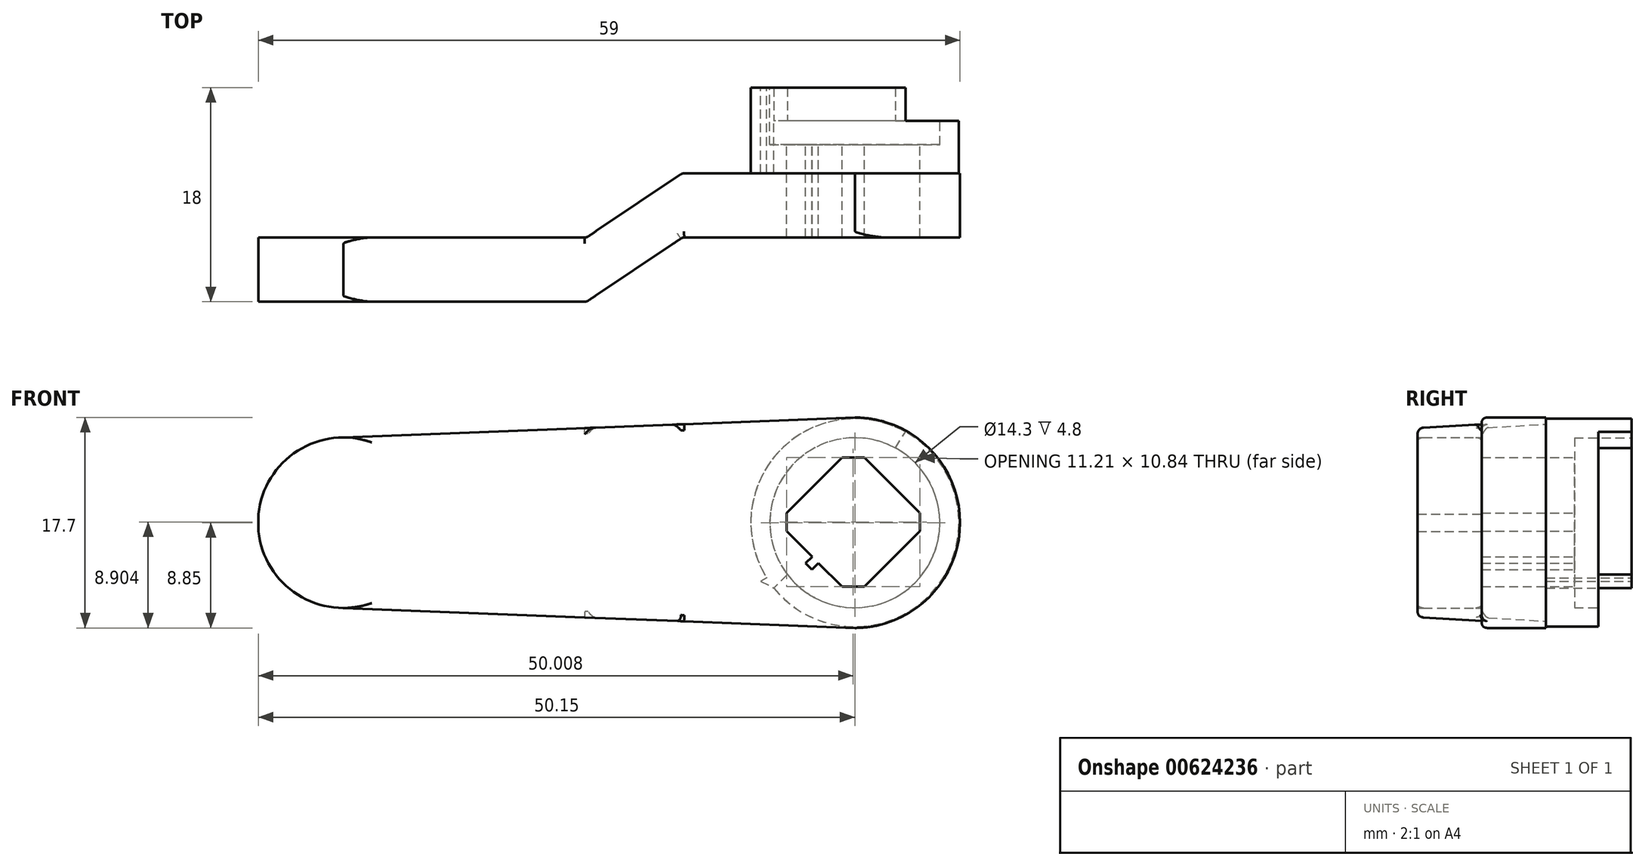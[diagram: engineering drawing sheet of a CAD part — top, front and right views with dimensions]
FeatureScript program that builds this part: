
annotation { "Feature Type Name" : "Feature", "Feature Type Description" : "" }
export const myFeature = defineFeature(function(context is Context, id is Id, definition is map)
    precondition{}
    {
        {
            var Q0;
            Q0=qCreatedBy(makeId("Top.planeOp"),FACE);
            var sketch = newSketch(context, id + "F0", { "sketchPlane" : qUnion([Q0])});
            skLineSegment(sketch, "E0", {"start": v(-29.5, 0) * mm, "end": v(29.5, 0) * mm, "construction": true});
            skLineSegment(sketch, "E1", {"start": v(0, 6.5) * mm, "end": v(0, -6.5) * mm, "construction": true});
            skLineSegment(sketch, "E2", {"start": v(-29.5, -6.5) * mm, "end": v(-29.5, -1.1) * mm});
            skLineSegment(sketch, "E3", {"start": v(-29.5, -6.5) * mm, "end": v(-1.9, -6.5) * mm});
            skLineSegment(sketch, "E4", {"start": v(-29.5, -1.1) * mm, "end": v(-1.9, -1.1) * mm});
            skLineSegment(sketch, "E5", {"start": v(-1.9, -1.1) * mm, "end": v(6.16, 4.3) * mm});
            skLineSegment(sketch, "E6", {"start": v(-1.9, -6.5) * mm, "end": v(6.16, -1.1) * mm});
            skLineSegment(sketch, "E7", {"start": v(6.16, 4.3) * mm, "end": v(29.5, 4.3) * mm});
            skLineSegment(sketch, "E8", {"start": v(29.5, 4.3) * mm, "end": v(29.5, -1.1) * mm});
            skLineSegment(sketch, "E9", {"start": v(29.5, -1.1) * mm, "end": v(6.16, -1.1) * mm});
            skSolve(sketch);
        }
        {
            var Q0;
            Q0=makeQuery(id+"F0.imprint","IMPRINT",FACE,{"disambiguationData":[TD([[makeQuery(id+"F0.imprint","IMPRINT",EDGE,{"derivedFrom":sQuery(id+"F0.wireOp",EDGE,"E2")}),-1.0]])]});
            extrude(context, id + "F1", {"entities" : qUnion([Q0]), "depth" : 17.7 * mm, "offsetDistance" : 25 * mm});
        }
        {
            var Q0;
            Q0=makeQuery(id+"F1.opExtrude","SWEPT_FACE",FACE,{"disambiguationData":[OSD([sQuery(id+"F0.wireOp",EDGE,"E7")])]});
            var sketch = newSketch(context, id + "F2", { "sketchPlane" : qUnion([Q0])});
            skLineSegment(sketch, "E10", {"start": v(-29.5, 8.85) * mm, "end": v(-20.65, 8.85) * mm, "construction": true});
            skArc(sketch, "E11", {"start": v(-20.65, 17.7) * mm, "mid": v(-29.5, 8.85) * mm, "end": v(-20.65, 0) * mm});
            skLineSegment(sketch, "E12", {"start": v(-20.65, 0) * mm, "end": v(-20.65, -1.09) * mm});
            skLineSegment(sketch, "E13", {"start": v(-20.65, -1.09) * mm, "end": v(-31.55, -1.09) * mm});
            skLineSegment(sketch, "E14", {"start": v(-31.55, -1.09) * mm, "end": v(-31.55, 8.85) * mm});
            skLineSegment(sketch, "E15.MirrorCS", {"start": v(-20.65, 17.7) * mm, "end": v(-20.65, 18.79) * mm});
            skLineSegment(sketch, "E16.MirrorCS", {"start": v(-20.65, 18.79) * mm, "end": v(-31.55, 18.79) * mm});
            skLineSegment(sketch, "E17.MirrorCS", {"start": v(-31.55, 18.79) * mm, "end": v(-31.55, 8.85) * mm});
            skLineSegment(sketch, "E18", {"start": v(-20.65, 0) * mm, "end": v(30.52, 0) * mm});
            skLineSegment(sketch, "E19", {"start": v(30.52, 0) * mm, "end": v(30.52, 2) * mm});
            skLineSegment(sketch, "E20", {"start": v(30.52, 2) * mm, "end": v(-20.65, 0) * mm});
            skLineSegment(sketch, "E21.MirrorCS", {"start": v(30.52, 15.7) * mm, "end": v(-20.65, 17.7) * mm});
            skLineSegment(sketch, "E22.MirrorCS", {"start": v(-20.65, 17.7) * mm, "end": v(30.52, 17.7) * mm});
            skLineSegment(sketch, "E23.MirrorCS", {"start": v(30.52, 17.7) * mm, "end": v(30.52, 15.7) * mm});
            skLineSegment(sketch, "E24", {"start": v(30.52, 2) * mm, "end": v(30.52, 15.7) * mm});
            skLineSegment(sketch, "E25", {"start": v(30.52, 8.85) * mm, "end": v(22.37, 8.85) * mm, "construction": true});
            skArc(sketch, "E26", {"start": v(22.37, 1.68) * mm, "mid": v(29.54, 8.85) * mm, "end": v(22.37, 16.02) * mm});
            skSolve(sketch);
        }
        {
            var Q0;
            {var subQ0=sQuery(id+"F2.wireOp",EDGE,"E24");Q0=makeQuery(id+"F2.imprint","IMPRINT",FACE,{"disambiguationData":[TD([[makeQuery(id+"F2.imprint","IMPRINT",EDGE,{"derivedFrom":subQ0}),1.0]])]});}
            var Q1;
            {var subQ1=sQuery(id+"F0.wireOp",EDGE,"E7");var subQ2=makeQuery(id+"F1.opExtrude","CAP_EDGE",EDGE,{"disambiguationData":[OSD([subQ1])],"isStart":false});var subQ4=makeQuery(id+"F1.opExtrude","SWEPT_EDGE",EDGE,{"disambiguationData":[OSD([subQ1,sQuery(id+"F0.wireOp",EDGE,"E8")])]});var subQ6=makeQuery(id+"F2.imprint","INTERSECT",VERTEX,{"derivedFrom":[subQ4,subQ2]});Q1=makeQuery(id+"F2.imprint","IMPRINT",FACE,{"disambiguationData":[TD([[makeQuery(id+"F2.imprint","IMPRINT",EDGE,{"disambiguationData":[TD([[subQ6,-1.0]])],"derivedFrom":subQ4}),1.0]])]});}
            var Q2;
            {var subQ1=sQuery(id+"F0.wireOp",EDGE,"E7");var subQ2=makeQuery(id+"F1.opExtrude","CAP_EDGE",EDGE,{"disambiguationData":[OSD([subQ1])],"isStart":true});var subQ4=makeQuery(id+"F1.opExtrude","SWEPT_EDGE",EDGE,{"disambiguationData":[OSD([subQ1,sQuery(id+"F0.wireOp",EDGE,"E8")])]});var subQ6=makeQuery(id+"F2.imprint","INTERSECT",VERTEX,{"derivedFrom":[subQ4,subQ2]});Q2=makeQuery(id+"F2.imprint","IMPRINT",FACE,{"disambiguationData":[TD([[makeQuery(id+"F2.imprint","IMPRINT",EDGE,{"disambiguationData":[TD([[subQ6,1.0]])],"derivedFrom":subQ4}),1.0]])]});}
            var Q3;
            {var subQ0=sQuery(id+"F2.wireOp",EDGE,"E18");var subQ1=sQuery(id+"F0.wireOp",EDGE,"E7");var subQ2=makeQuery(id+"F1.opExtrude","SWEPT_EDGE",EDGE,{"disambiguationData":[OSD([sQuery(id+"F0.wireOp",EDGE,"E5"),subQ1])]});var subQ3=makeQuery(id+"F2.imprint","INTERSECT",VERTEX,{"derivedFrom":[subQ2,subQ0]});Q3=makeQuery(id+"F2.imprint","IMPRINT",FACE,{"disambiguationData":[TD([[makeQuery(id+"F2.imprint","IMPRINT",EDGE,{"disambiguationData":[TD([[subQ3,1.0]])],"derivedFrom":subQ2}),-1.0]])]});}
            var Q4;
            {var subQ0=sQuery(id+"F2.wireOp",EDGE,"E22.MirrorCS");var subQ2=sQuery(id+"F0.wireOp",EDGE,"E7");var subQ4=makeQuery(id+"F1.opExtrude","SWEPT_EDGE",EDGE,{"disambiguationData":[OSD([sQuery(id+"F0.wireOp",EDGE,"E5"),subQ2])]});var subQ6=makeQuery(id+"F2.imprint","INTERSECT",VERTEX,{"derivedFrom":[subQ4,subQ0]});Q4=makeQuery(id+"F2.imprint","IMPRINT",FACE,{"disambiguationData":[TD([[makeQuery(id+"F2.imprint","IMPRINT",EDGE,{"disambiguationData":[TD([[subQ6,-1.0]])],"derivedFrom":subQ4}),-1.0]])]});}
            var Q5;
            {var subQ0=sQuery(id+"F2.wireOp",EDGE,"E23.MirrorCS");Q5=makeQuery(id+"F2.imprint","IMPRINT",FACE,{"disambiguationData":[TD([[makeQuery(id+"F2.imprint","IMPRINT",EDGE,{"derivedFrom":subQ0}),-1.0]])]});}
            var Q6;
            {var subQ8=sQuery(id+"F2.wireOp",EDGE,"E12");Q6=makeQuery(id+"F2.imprint","IMPRINT",FACE,{"disambiguationData":[TD([[makeQuery(id+"F2.imprint","IMPRINT",EDGE,{"derivedFrom":subQ8}),-1.0]])]});}
            var Q7;
            {var subQ5=sQuery(id+"F2.wireOp",EDGE,"E19");Q7=makeQuery(id+"F2.imprint","IMPRINT",FACE,{"disambiguationData":[TD([[makeQuery(id+"F2.imprint","IMPRINT",EDGE,{"derivedFrom":subQ5}),1.0]])]});}
            extrude(context, id + "F3", {"entities" : qUnion([Q0, Q1, Q2, Q3, Q4, Q5, Q6, Q7]), "operationType" : NewBodyOperationType.REMOVE, "endBound" : BoundingType.THROUGH_ALL, "oppositeDirection" : true, "depth" : 15 * mm, "offsetDistance" : 25 * mm});
        }
        {
            var Q0;
            Q0=makeQuery(id+"F1.opExtrude","SWEPT_FACE",FACE,{"disambiguationData":[OSD([sQuery(id+"F0.wireOp",EDGE,"E7")])]});
            var sketch = newSketch(context, id + "F4", { "sketchPlane" : qUnion([Q0])});
            skCircle(sketch, "E27", {"center": v(-20.65, 8.85) * mm, "radius": 8.75 * mm});
            skSolve(sketch);
        }
        {
            var Q0;
            Q0 = qSketchRegion(id + "F4", true);
            extrude(context, id + "F5", {"entities" : qUnion([Q0]), "operationType" : NewBodyOperationType.ADD, "depth" : 4.4 * mm, "offsetDistance" : 25 * mm});
        }
        {
            var Q0;
            Q0=makeQuery(id+"F5.opExtrude","CAP_FACE",FACE,{"disambiguationData":[OSD([sQuery(id+"F4.wireOp",EDGE,"E27")])],"isStart":false});
            var sketch = newSketch(context, id + "F6", { "sketchPlane" : qUnion([Q0])});
            skCircle(sketch, "E28", {"center": v(-20.65, 8.85) * mm, "radius": 7.15 * mm});
            skSolve(sketch);
        }
        {
            var Q0;
            Q0 = qSketchRegion(id + "F6", true);
            extrude(context, id + "F7", {"entities" : qUnion([Q0]), "operationType" : NewBodyOperationType.REMOVE, "oppositeDirection" : true, "depth" : 2 * mm, "offsetDistance" : 25 * mm});
        }
        {
            var Q0;
            Q0=makeQuery(id+"F7.boolean.opBoolean","COPY",FACE,{"derivedFrom":makeQuery(id+"F7.opExtrude","CAP_FACE",FACE,{"disambiguationData":[OSD([sQuery(id+"F6.wireOp",EDGE,"E28")])],"isStart":false})});
            var sketch = newSketch(context, id + "F8", { "sketchPlane" : qUnion([Q0])});
            skLineSegment(sketch, "E29", {"start": v(-20.5, 2.54) * mm, "end": v(-26.87, 8.9) * mm});
            skLineSegment(sketch, "E30", {"start": v(-26.87, 8.9) * mm, "end": v(-20.5, 15.27) * mm});
            skLineSegment(sketch, "E31", {"start": v(-13.5, 8.9) * mm, "end": v(-27.8, 8.9) * mm, "construction": true});
            skLineSegment(sketch, "E32", {"start": v(-20.5, 2.54) * mm, "end": v(-20.5, 15.27) * mm, "construction": true});
            skLineSegment(sketch, "E33.MirrorCS", {"start": v(-20.5, 2.54) * mm, "end": v(-14.14, 8.9) * mm});
            skLineSegment(sketch, "E34.MirrorCS", {"start": v(-14.14, 8.9) * mm, "end": v(-20.5, 15.27) * mm});
            skLineSegment(sketch, "E35", {"start": v(-19.57, 3.48) * mm, "end": v(-21.45, 3.48) * mm});
            skLineSegment(sketch, "E36", {"start": v(-26.11, 8.14) * mm, "end": v(-26.11, 9.67) * mm});
            skLineSegment(sketch, "E37.MirrorCS", {"start": v(-19.57, 14.33) * mm, "end": v(-21.45, 14.33) * mm});
            skLineSegment(sketch, "E38.MirrorCS", {"start": v(-14.9, 8.14) * mm, "end": v(-14.9, 9.67) * mm});
            skLineSegment(sketch, "E39", {"start": v(-23.7, 12.09) * mm, "end": v(-17.33, 5.72) * mm, "construction": true});
            skLineSegment(sketch, "E40", {"start": v(-17.33, 5.72) * mm, "end": v(-16.78, 5.17) * mm, "construction": true});
            skLineSegment(sketch, "E41", {"start": v(-16.78, 5.17) * mm, "end": v(-17.04, 4.9) * mm});
            skLineSegment(sketch, "E42", {"start": v(-17.04, 4.9) * mm, "end": v(-17.59, 5.46) * mm});
            skLineSegment(sketch, "E43.MirrorCS", {"start": v(-16.78, 5.17) * mm, "end": v(-16.51, 5.43) * mm});
            skLineSegment(sketch, "E44.MirrorCS", {"start": v(-16.51, 5.43) * mm, "end": v(-17.06, 5.98) * mm});
            skSolve(sketch);
        }
        {
            var Q0;
            {var subQ3=sQuery(id+"F8.wireOp",EDGE,"E35");Q0=makeQuery(id+"F8.imprint","IMPRINT",FACE,{"disambiguationData":[TD([[makeQuery(id+"F8.imprint","IMPRINT",EDGE,{"derivedFrom":subQ3}),-1.0]])]});}
            var Q1;
            Q1=makeQuery(id+"F8.imprint","IMPRINT",FACE,{"disambiguationData":[TD([[makeQuery(id+"F8.imprint","IMPRINT",EDGE,{"derivedFrom":sQuery(id+"F8.wireOp",EDGE,"E41")}),-1.0]])]});
            extrude(context, id + "F9", {"entities" : qUnion([Q0, Q1]), "operationType" : NewBodyOperationType.REMOVE, "endBound" : BoundingType.THROUGH_ALL, "oppositeDirection" : true, "depth" : 25 * mm, "offsetDistance" : 25 * mm});
        }
        {
            var Q0;
            Q0=makeQuery(id+"F5.opExtrude","CAP_FACE",FACE,{"disambiguationData":[OSD([sQuery(id+"F4.wireOp",EDGE,"E27")])],"isStart":false});
            var sketch = newSketch(context, id + "F10", { "sketchPlane" : qUnion([Q0])});
            skLineSegment(sketch, "E45", {"start": v(-14.98, 4.5) * mm, "end": v(-14.98, 4.5) * mm});
            skLineSegment(sketch, "E46", {"start": v(-24.06, 15.13) * mm, "end": v(-24.9, 16.5) * mm});
            skLineSegment(sketch, "E47", {"start": v(-14.98, 4.5) * mm, "end": v(-13.84, 3.35) * mm});
            skArc(sketch, "E48", {"start": v(-13.84, 3.35) * mm, "mid": v(-13.96, 14.48) * mm, "end": v(-24.9, 16.5) * mm});
            skArc(sketch, "E49", {"start": v(-14.98, 4.5) * mm, "mid": v(-15.21, 13.5) * mm, "end": v(-24.06, 15.13) * mm});
            skSolve(sketch);
        }
        {
            var Q0;
            Q0 = qSketchRegion(id + "F10", true);
            extrude(context, id + "F11", {"entities" : qUnion([Q0]), "operationType" : NewBodyOperationType.ADD, "depth" : 2.8 * mm, "offsetDistance" : 25 * mm});
        }
        {
            var Q0;
            Q0=makeQuery(id+"F11.opExtrude","CAP_FACE",FACE,{"disambiguationData":[OSD([sQuery(id+"F10.wireOp",EDGE,"E46"),sQuery(id+"F10.wireOp",EDGE,"E47"),sQuery(id+"F10.wireOp",EDGE,"E48"),sQuery(id+"F10.wireOp",EDGE,"E49")])],"isStart":false});
            var sketch = newSketch(context, id + "F12", { "sketchPlane" : qUnion([Q0])});
            skLineSegment(sketch, "E50", {"start": v(-13.84, 3.35) * mm, "end": v(-12.7, 3.93) * mm});
            skLineSegment(sketch, "E51", {"start": v(-12.7, 3.93) * mm, "end": v(-13.24, 4.2) * mm});
            skLineSegment(sketch, "E52", {"start": v(-13.24, 4.2) * mm, "end": v(-13.84, 3.35) * mm});
            skSolve(sketch);
        }
        {
            var Q0;
            Q0 = qSketchRegion(id + "F12", true);
            var Q1;
            Q1=makeQuery(id+"F1.opExtrude","SWEPT_FACE",FACE,{"disambiguationData":[OSD([sQuery(id+"F0.wireOp",EDGE,"E7")])]});
            extrude(context, id + "F13", {"entities" : qUnion([Q0]), "operationType" : NewBodyOperationType.ADD, "endBound" : BoundingType.UP_TO_SURFACE, "oppositeDirection" : true, "depth" : 25 * mm, "endBoundEntityFace" : qUnion([Q1]), "offsetDistance" : 25 * mm});
        }
        {
            var Q0;
            Q0=makeQuery(id+"F3.boolean.opBoolean","INTERSECT",EDGE,{"derivedFrom":[makeQuery(id+"F1.opExtrude","SWEPT_FACE",FACE,{"disambiguationData":[OSD([sQuery(id+"F0.wireOp",EDGE,"E4")])]}),makeQuery(id+"F3.opExtrude","SWEPT_FACE",FACE,{"disambiguationData":[OSD([sQuery(id+"F2.wireOp",EDGE,"E21.MirrorCS")])]})]});
            var Q1;
            Q1=makeQuery(id+"F1.opExtrude","SWEPT_EDGE",EDGE,{"disambiguationData":[OSD([sQuery(id+"F0.wireOp",EDGE,"E4"),sQuery(id+"F0.wireOp",EDGE,"E5")])]});
            var Q2;
            Q2=makeQuery(id+"F1.opExtrude","SWEPT_EDGE",EDGE,{"disambiguationData":[OSD([sQuery(id+"F0.wireOp",EDGE,"E5"),sQuery(id+"F0.wireOp",EDGE,"E7")])]});
            var Q3;
            Q3=makeQuery(id+"F3.boolean.opBoolean","INTERSECT",EDGE,{"derivedFrom":[makeQuery(id+"F1.opExtrude","SWEPT_FACE",FACE,{"disambiguationData":[OSD([sQuery(id+"F0.wireOp",EDGE,"E4")])]}),makeQuery(id+"F3.opExtrude","SWEPT_FACE",FACE,{"disambiguationData":[OSD([sQuery(id+"F2.wireOp",EDGE,"E20")])]})]});
            var Q4;
            Q4=makeQuery(id+"F3.boolean.opBoolean","COPY",EDGE,{"derivedFrom":makeQuery(id+"F3.opExtrude","CAP_EDGE",EDGE,{"disambiguationData":[OSD([sQuery(id+"F2.wireOp",EDGE,"E20")])],"isStart":true})});
            var Q5;
            Q5=makeQuery(id+"F3.boolean.opBoolean","COPY",EDGE,{"derivedFrom":makeQuery(id+"F3.opExtrude","CAP_EDGE",EDGE,{"disambiguationData":[OSD([sQuery(id+"F2.wireOp",EDGE,"E21.MirrorCS")])],"isStart":true})});
            var Q6;
            Q6=makeQuery(id+"F3.boolean.opBoolean","COPY",EDGE,{"derivedFrom":makeQuery(id+"F3.opExtrude","CAP_EDGE",EDGE,{"disambiguationData":[OSD([sQuery(id+"F2.wireOp",EDGE,"E11")])],"isStart":true})});
            var Q7;
            Q7=makeQuery(id+"F3.boolean.opBoolean","INTERSECT",EDGE,{"derivedFrom":[makeQuery(id+"F1.opExtrude","SWEPT_FACE",FACE,{"disambiguationData":[OSD([sQuery(id+"F0.wireOp",EDGE,"E9")])]}),makeQuery(id+"F3.opExtrude","SWEPT_FACE",FACE,{"disambiguationData":[OSD([sQuery(id+"F2.wireOp",EDGE,"E21.MirrorCS")])]})]});
            var Q8;
            Q8=makeQuery(id+"F3.boolean.opBoolean","INTERSECT",EDGE,{"derivedFrom":[makeQuery(id+"F1.opExtrude","SWEPT_FACE",FACE,{"disambiguationData":[OSD([sQuery(id+"F0.wireOp",EDGE,"E9")])]}),makeQuery(id+"F3.opExtrude","SWEPT_FACE",FACE,{"disambiguationData":[OSD([sQuery(id+"F2.wireOp",EDGE,"E20")])]})]});
            var Q9;
            Q9=makeQuery(id+"F1.opExtrude","SWEPT_EDGE",EDGE,{"disambiguationData":[OSD([sQuery(id+"F0.wireOp",EDGE,"E6"),sQuery(id+"F0.wireOp",EDGE,"E9")])]});
            var Q10;
            Q10=makeQuery(id+"F3.boolean.opBoolean","INTERSECT",EDGE,{"derivedFrom":[makeQuery(id+"F1.opExtrude","SWEPT_FACE",FACE,{"disambiguationData":[OSD([sQuery(id+"F0.wireOp",EDGE,"E6")])]}),makeQuery(id+"F3.opExtrude","SWEPT_FACE",FACE,{"disambiguationData":[OSD([sQuery(id+"F2.wireOp",EDGE,"E20")])]})]});
            var Q11;
            Q11=makeQuery(id+"F1.opExtrude","SWEPT_EDGE",EDGE,{"disambiguationData":[OSD([sQuery(id+"F0.wireOp",EDGE,"E3"),sQuery(id+"F0.wireOp",EDGE,"E6")])]});
            var Q12;
            Q12=makeQuery(id+"F3.boolean.opBoolean","INTERSECT",EDGE,{"derivedFrom":[makeQuery(id+"F1.opExtrude","SWEPT_FACE",FACE,{"disambiguationData":[OSD([sQuery(id+"F0.wireOp",EDGE,"E3")])]}),makeQuery(id+"F3.opExtrude","SWEPT_FACE",FACE,{"disambiguationData":[OSD([sQuery(id+"F2.wireOp",EDGE,"E20")])]})]});
            var Q13;
            Q13=makeQuery(id+"F3.boolean.opBoolean","INTERSECT",EDGE,{"derivedFrom":[makeQuery(id+"F1.opExtrude","SWEPT_FACE",FACE,{"disambiguationData":[OSD([sQuery(id+"F0.wireOp",EDGE,"E3")])]}),makeQuery(id+"F3.opExtrude","SWEPT_FACE",FACE,{"disambiguationData":[OSD([sQuery(id+"F2.wireOp",EDGE,"E21.MirrorCS")])]})]});
            fillet(context, id + "F14", {"entities" : qUnion([Q0, Q1, Q2, Q3, Q4, Q5, Q6, Q7, Q8, Q9, Q10, Q11, Q12, Q13]), "radius" : 0.5 * mm, "tangentPropagation" : true, "allowEdgeOverflow" : false});
        }
    });
